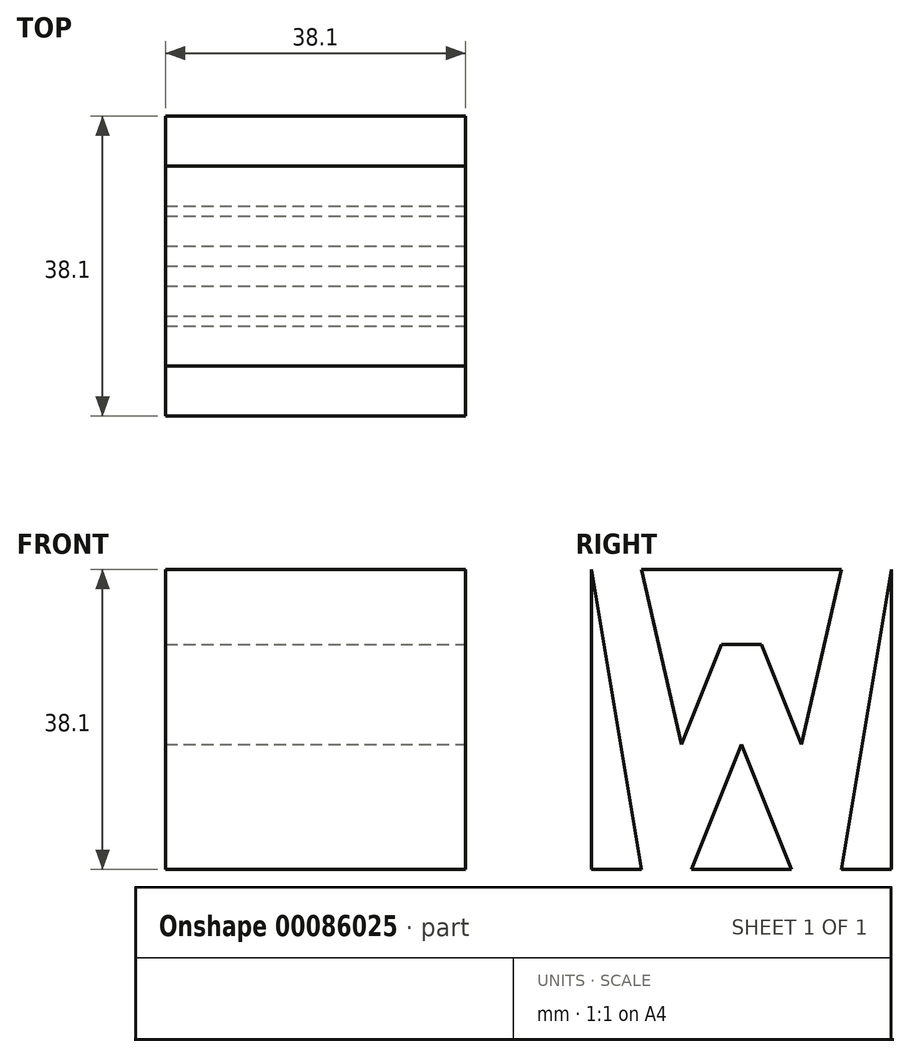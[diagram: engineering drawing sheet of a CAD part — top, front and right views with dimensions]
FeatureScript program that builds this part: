
annotation { "Feature Type Name" : "Feature", "Feature Type Description" : "" }
export const myFeature = defineFeature(function(context is Context, id is Id, definition is map)
    precondition{}
    {
        {
            var Q0;
            Q0=qCreatedBy(makeId("Front.planeOp"),FACE);
            var sketch = newSketch(context, id + "F0", { "sketchPlane" : qUnion([Q0])});
            skLineSegment(sketch, "E0", {"start": v(0, 0) * mm, "end": v(0, 38.1) * mm});
            skLineSegment(sketch, "E1", {"start": v(0, 38.1) * mm, "end": v(38.1, 38.1) * mm});
            skLineSegment(sketch, "E2", {"start": v(38.1, 38.1) * mm, "end": v(38.1, 0) * mm});
            skLineSegment(sketch, "E3", {"start": v(38.1, 0) * mm, "end": v(0, 0) * mm});
            skSolve(sketch);
        }
        {
            var Q0;
            Q0=makeQuery(id+"F0.imprint","IMPRINT",FACE,{"disambiguationData":[TD([[makeQuery(id+"F0.imprint","IMPRINT",EDGE,{"derivedFrom":sQuery(id+"F0.wireOp",EDGE,"E0")}),-1.0]])]});
            extrude(context, id + "F1", {"entities" : qUnion([Q0]), "depth" : 38.1 * mm});
        }
        {
            var Q0;
            Q0=qCreatedBy(makeId("Front.planeOp"),FACE);
            cPlane(context, id + "F2", {"entities" : qUnion([Q0]), "cplaneType" : CPlaneType.OFFSET, "offset" : 38.1 * mm, "width" : 152.4 * mm, "height" : 152.4 * mm});
        }
        {
            var Q0;
            Q0=qCreatedBy(makeId("Right.planeOp"),FACE);
            cPlane(context, id + "F3", {"entities" : qUnion([Q0]), "cplaneType" : CPlaneType.OFFSET, "offset" : 38.1 * mm, "width" : 152.4 * mm, "height" : 152.4 * mm});
        }
        {
            var Q0;
            Q0=qCreatedBy(id+"F3.planeOp",FACE);
            var sketch = newSketch(context, id + "F4", { "sketchPlane" : qUnion([Q0])});
            skLineSegment(sketch, "E4", {"start": v(-38.1, 0) * mm, "end": v(0, 0) * mm});
            skLineSegment(sketch, "E5", {"start": v(0, 0) * mm, "end": v(0, 38.1) * mm});
            skLineSegment(sketch, "E6", {"start": v(0, 38.1) * mm, "end": v(-38.1, 38.1) * mm});
            skLineSegment(sketch, "E7", {"start": v(-38.1, 38.1) * mm, "end": v(-38.1, 0) * mm});
            skLineSegment(sketch, "E8", {"start": v(-38.1, 38.1) * mm, "end": v(-31.75, 0) * mm});
            skLineSegment(sketch, "E9", {"start": v(-31.75, 0) * mm, "end": v(-25.4, 0) * mm});
            skLineSegment(sketch, "E10", {"start": v(-25.4, 0) * mm, "end": v(-19.05, 15.88) * mm});
            skLineSegment(sketch, "E11", {"start": v(-19.05, 15.88) * mm, "end": v(-12.7, 0) * mm});
            skLineSegment(sketch, "E12", {"start": v(-12.7, 0) * mm, "end": v(-6.35, 0) * mm});
            skLineSegment(sketch, "E13", {"start": v(-6.35, 0) * mm, "end": v(0, 38.1) * mm});
            skLineSegment(sketch, "E14", {"start": v(-6.35, 38.1) * mm, "end": v(-11.43, 15.88) * mm});
            skLineSegment(sketch, "E15", {"start": v(-11.43, 15.88) * mm, "end": v(-16.51, 28.58) * mm});
            skLineSegment(sketch, "E16", {"start": v(-16.51, 28.58) * mm, "end": v(-21.6, 28.58) * mm});
            skLineSegment(sketch, "E17", {"start": v(-21.6, 28.58) * mm, "end": v(-26.67, 15.87) * mm});
            skLineSegment(sketch, "E18", {"start": v(-26.67, 15.88) * mm, "end": v(-31.75, 38.1) * mm});
            skLineSegment(sketch, "E19", {"start": v(-31.75, 38.1) * mm, "end": v(-38.1, 38.1) * mm});
            skSolve(sketch);
        }
        {
            var Q0;
            Q0=makeQuery(id+"F4.imprint","IMPRINT",FACE,{"disambiguationData":[TD([[makeQuery(id+"F4.imprint","IMPRINT",EDGE,{"derivedFrom":sQuery(id+"F4.wireOp",EDGE,"E8")}),1.0]])]});
            extrude(context, id + "F5", {"entities" : qUnion([Q0]), "operationType" : NewBodyOperationType.REMOVE, "oppositeDirection" : true, "depth" : 38.1 * mm});
        }
    });
